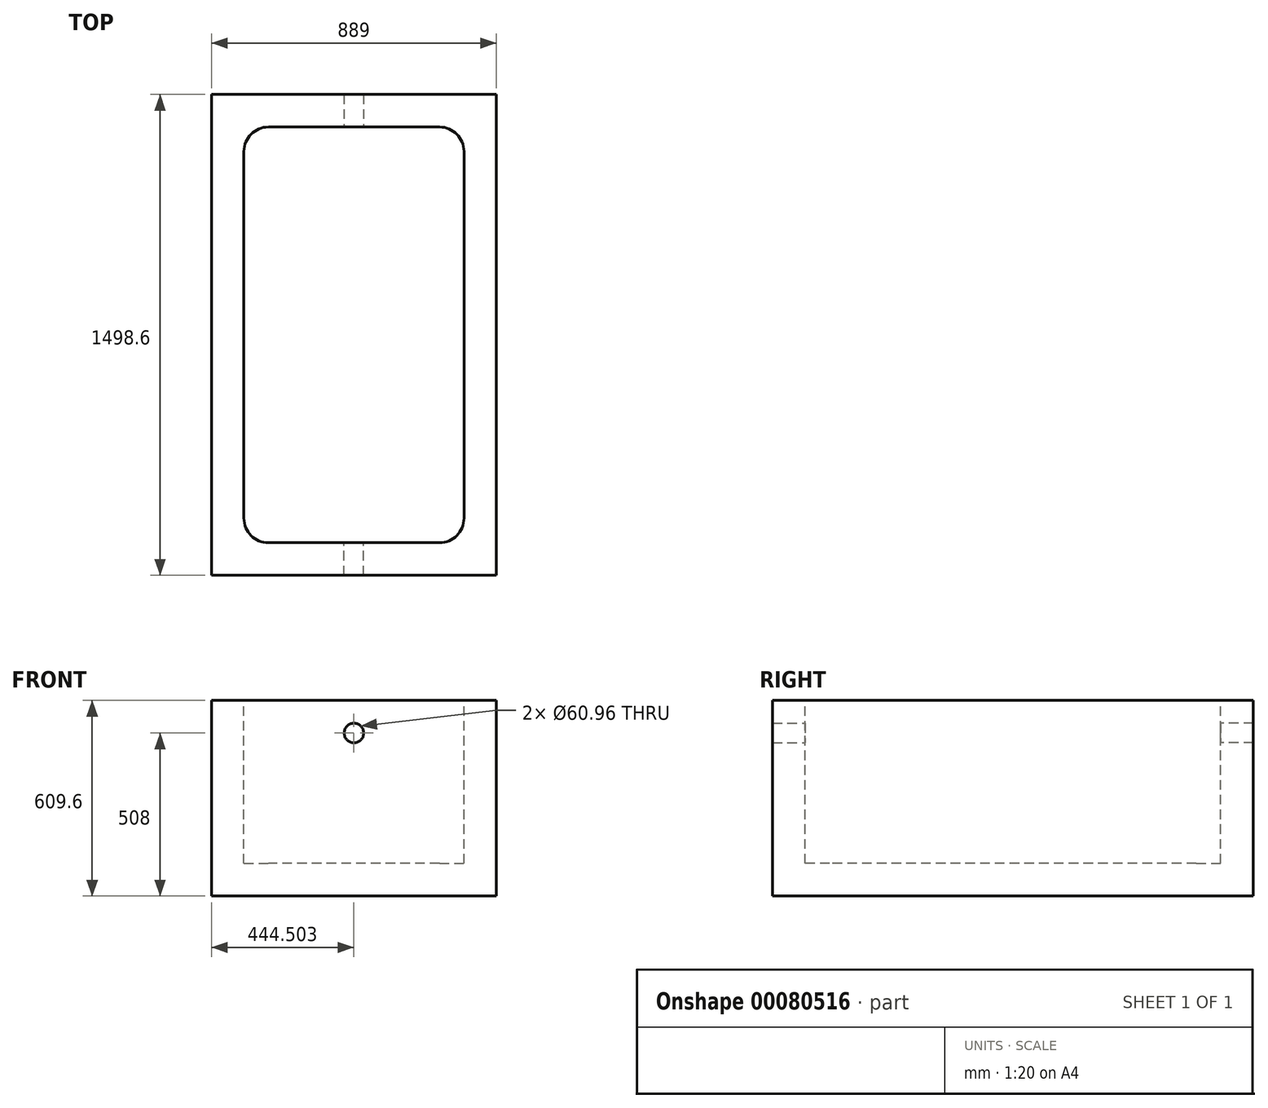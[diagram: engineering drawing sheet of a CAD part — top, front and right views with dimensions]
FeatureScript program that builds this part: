
annotation { "Feature Type Name" : "Feature", "Feature Type Description" : "" }
export const myFeature = defineFeature(function(context is Context, id is Id, definition is map)
    precondition{}
    {
        {
            var Q0;
            Q0=qCreatedBy(makeId("Top.planeOp"),FACE);
            var sketch = newSketch(context, id + "F0", { "sketchPlane" : qUnion([Q0])});
            skLineSegment(sketch, "E0.bottom", {"start": v(-1038.76, -765.34) * mm, "end": v(-149.76, -765.34) * mm});
            skLineSegment(sketch, "E0.top", {"start": v(-1038.76, 733.26) * mm, "end": v(-149.76, 733.26) * mm});
            skLineSegment(sketch, "E0.left", {"start": v(-1038.76, -765.34) * mm, "end": v(-1038.76, 733.26) * mm});
            skLineSegment(sketch, "E0.right", {"start": v(-149.76, -765.34) * mm, "end": v(-149.76, 733.26) * mm});
            skSolve(sketch);
        }
        {
            var Q0;
            Q0=makeQuery(id+"F0.imprint","IMPRINT",FACE,{"disambiguationData":[TD([[makeQuery(id+"F0.imprint","IMPRINT",EDGE,{"derivedFrom":sQuery(id+"F0.wireOp",EDGE,"E0.bottom")}),1.0]])]});
            extrude(context, id + "F1", {"entities" : qUnion([Q0]), "depth" : 609.6 * mm});
        }
        {
            var Q0;
            Q0=makeQuery(id+"F1.opExtrude","CAP_FACE",FACE,{"disambiguationData":[OSD([sQuery(id+"F0.wireOp",EDGE,"E0.bottom"),sQuery(id+"F0.wireOp",EDGE,"E0.top"),sQuery(id+"F0.wireOp",EDGE,"E0.left"),sQuery(id+"F0.wireOp",EDGE,"E0.right")])],"isStart":false});
            var sketch = newSketch(context, id + "F2", { "sketchPlane" : qUnion([Q0])});
            skLineSegment(sketch, "E1.bottom", {"start": v(-251.36, 631.66) * mm, "end": v(-937.16, 631.66) * mm});
            skLineSegment(sketch, "E1.top", {"start": v(-251.36, -663.74) * mm, "end": v(-937.16, -663.74) * mm});
            skLineSegment(sketch, "E1.left", {"start": v(-251.36, 631.66) * mm, "end": v(-251.36, -663.74) * mm});
            skLineSegment(sketch, "E1.right", {"start": v(-937.16, 631.66) * mm, "end": v(-937.16, -663.74) * mm});
            skSolve(sketch);
        }
        {
            var Q0;
            Q0=makeQuery(id+"F2.imprint","IMPRINT",FACE,{"disambiguationData":[TD([[makeQuery(id+"F2.imprint","IMPRINT",EDGE,{"derivedFrom":sQuery(id+"F2.wireOp",EDGE,"E1.bottom")}),1.0]])]});
            extrude(context, id + "F3", {"entities" : qUnion([Q0]), "operationType" : NewBodyOperationType.REMOVE, "oppositeDirection" : true, "depth" : 508 * mm});
        }
        {
            var Q0;
            Q0=makeQuery(id+"F3.boolean.opBoolean","COPY",EDGE,{"derivedFrom":makeQuery(id+"F3.opExtrude","SWEPT_EDGE",EDGE,{"disambiguationData":[OSD([sQuery(id+"F2.wireOp",EDGE,"E1.bottom"),sQuery(id+"F2.wireOp",EDGE,"E1.right")])]})});
            fillet(context, id + "F4", {"entities" : qUnion([Q0]), "radius" : 76.2 * mm, "tangentPropagation" : true, "allowEdgeOverflow" : false});
        }
        {
            var Q0;
            Q0=makeQuery(id+"F3.boolean.opBoolean","COPY",EDGE,{"derivedFrom":makeQuery(id+"F3.opExtrude","SWEPT_EDGE",EDGE,{"disambiguationData":[OSD([sQuery(id+"F2.wireOp",EDGE,"E1.bottom"),sQuery(id+"F2.wireOp",EDGE,"E1.left")])]})});
            fillet(context, id + "F5", {"entities" : qUnion([Q0]), "radius" : 76.2 * mm, "tangentPropagation" : true, "allowEdgeOverflow" : false});
        }
        {
            var Q0;
            Q0=makeQuery(id+"F3.boolean.opBoolean","COPY",EDGE,{"derivedFrom":makeQuery(id+"F3.opExtrude","SWEPT_EDGE",EDGE,{"disambiguationData":[OSD([sQuery(id+"F2.wireOp",EDGE,"E1.top"),sQuery(id+"F2.wireOp",EDGE,"E1.left")])]})});
            fillet(context, id + "F6", {"entities" : qUnion([Q0]), "radius" : 76.2 * mm, "tangentPropagation" : true, "allowEdgeOverflow" : false});
        }
        {
            var Q0;
            Q0=makeQuery(id+"F3.boolean.opBoolean","COPY",EDGE,{"derivedFrom":makeQuery(id+"F3.opExtrude","SWEPT_EDGE",EDGE,{"disambiguationData":[OSD([sQuery(id+"F2.wireOp",EDGE,"E1.top"),sQuery(id+"F2.wireOp",EDGE,"E1.right")])]})});
            fillet(context, id + "F7", {"entities" : qUnion([Q0]), "radius" : 76.2 * mm, "tangentPropagation" : true, "allowEdgeOverflow" : false});
        }
        {
            var Q0;
            Q0=makeQuery(id+"F3.boolean.opBoolean","COPY",FACE,{"derivedFrom":makeQuery(id+"F3.opExtrude","SWEPT_FACE",FACE,{"disambiguationData":[OSD([sQuery(id+"F2.wireOp",EDGE,"E1.bottom")])]})});
            var sketch = newSketch(context, id + "F8", { "sketchPlane" : qUnion([Q0])});
            skCircle(sketch, "E2", {"center": v(-594.26, 508) * mm, "radius": 30.48 * mm});
            skSolve(sketch);
        }
        {
            var Q0;
            Q0=sQuery(id+"F8.wireOp",VERTEX,"E2.center");
            var Q1;
            Q1=makeQuery(id+"F1.opExtrude","SWEPT_BODY",BODY,{"disambiguationData":[OSD([sQuery(id+"F0.wireOp",EDGE,"E0.bottom"),sQuery(id+"F0.wireOp",EDGE,"E0.top"),sQuery(id+"F0.wireOp",EDGE,"E0.left"),sQuery(id+"F0.wireOp",EDGE,"E0.right")])]});
            hole(context, id + "F9", {"style" : HoleStyle.SIMPLE, "endStyle" : HoleEndStyle.THROUGH, "holeDiameter" : 60.96 * mm, "locations" : qUnion([Q0]), "scope" : qUnion([Q1]), "isTappedThrough" : true});
        }
        {
            var Q0;
            Q0=makeQuery(id+"F3.boolean.opBoolean","COPY",FACE,{"derivedFrom":makeQuery(id+"F3.opExtrude","SWEPT_FACE",FACE,{"disambiguationData":[OSD([sQuery(id+"F2.wireOp",EDGE,"E1.top")])]})});
            var sketch = newSketch(context, id + "F10", { "sketchPlane" : qUnion([Q0])});
            skCircle(sketch, "E3", {"center": v(594.26, 508) * mm, "radius": 30.48 * mm});
            skSolve(sketch);
        }
        {
            var Q0;
            Q0=sQuery(id+"F10.wireOp",VERTEX,"E3.center");
            var Q1;
            Q1=makeQuery(id+"F1.opExtrude","SWEPT_BODY",BODY,{"disambiguationData":[OSD([sQuery(id+"F0.wireOp",EDGE,"E0.bottom"),sQuery(id+"F0.wireOp",EDGE,"E0.top"),sQuery(id+"F0.wireOp",EDGE,"E0.left"),sQuery(id+"F0.wireOp",EDGE,"E0.right")])]});
            hole(context, id + "F11", {"style" : HoleStyle.SIMPLE, "endStyle" : HoleEndStyle.THROUGH, "holeDiameter" : 60.96 * mm, "locations" : qUnion([Q0]), "scope" : qUnion([Q1]), "isTappedThrough" : true});
        }
    });
